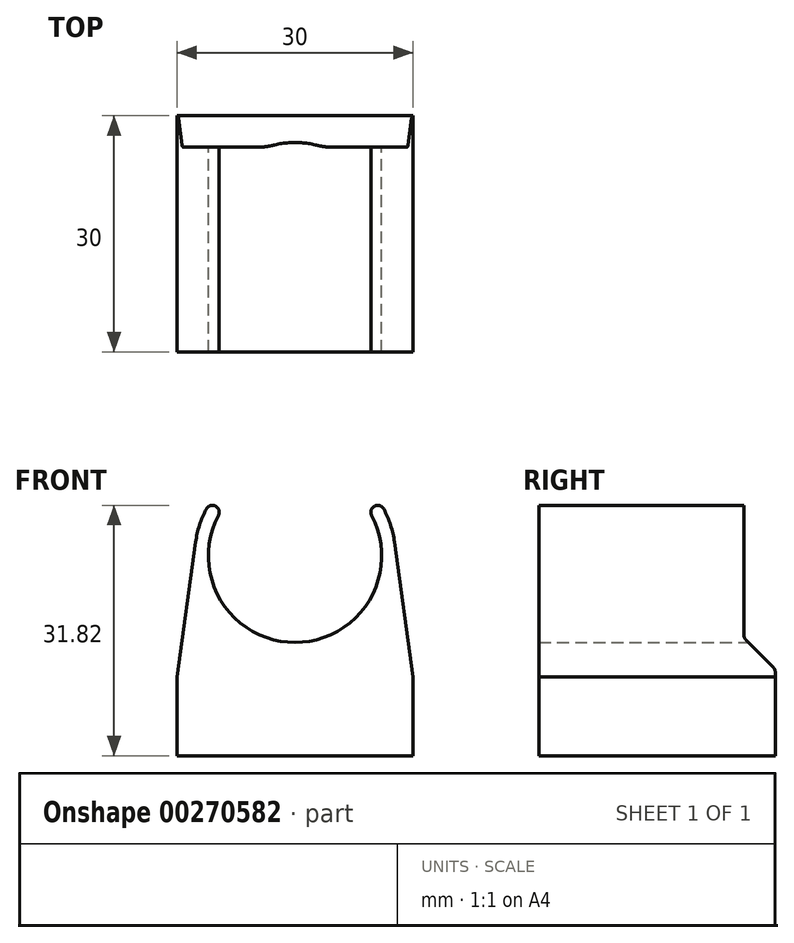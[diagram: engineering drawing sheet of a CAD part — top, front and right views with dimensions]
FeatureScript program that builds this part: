
annotation { "Feature Type Name" : "Feature", "Feature Type Description" : "" }
export const myFeature = defineFeature(function(context is Context, id is Id, definition is map)
    precondition{}
    {
        {
            var Q0;
            Q0=qCreatedBy(makeId("Front.planeOp"),FACE);
            var sketch = newSketch(context, id + "F0", { "sketchPlane" : qUnion([Q0])});
            skLineSegment(sketch, "E0.bottom", {"start": v(-15, 0) * mm, "end": v(15, 0) * mm});
            skLineSegment(sketch, "E0.top", {"start": v(-15, 10) * mm, "end": v(15, 10) * mm, "construction": true});
            skLineSegment(sketch, "E0.left", {"start": v(-15, 0) * mm, "end": v(-15, 10) * mm});
            skLineSegment(sketch, "E0.right", {"start": v(15, 0) * mm, "end": v(15, 10) * mm});
            skLineSegment(sketch, "E1", {"start": v(0, 10) * mm, "end": v(0, 14.4) * mm, "construction": true});
            skPoint(sketch, "E1.endSnap0", {"position": v(0, 10) * mm});
            skArc(sketch, "E2", {"start": v(-9.73, 30.54) * mm, "mid": v(0, 14.4) * mm, "end": v(9.73, 30.54) * mm});
            skArc(sketch, "E3", {"start": v(12.63, 27.15) * mm, "mid": v(12.14, 29.3) * mm, "end": v(11.27, 31.36) * mm});
            skLineSegment(sketch, "E4", {"start": v(-15, 10) * mm, "end": v(-12.63, 27.15) * mm});
            skLineSegment(sketch, "E5", {"start": v(15, 10) * mm, "end": v(12.63, 27.15) * mm});
            skArc(sketch, "E6", {"start": v(-9.73, 30.54) * mm, "mid": v(-10.1, 31.72) * mm, "end": v(-11.27, 31.36) * mm});
            skArc(sketch, "E7", {"start": v(11.27, 31.36) * mm, "mid": v(10.1, 31.72) * mm, "end": v(9.73, 30.54) * mm});
            skLineSegment(sketch, "E8", {"start": v(-9.63, 35.6) * mm, "end": v(-9.63, 27.49) * mm, "construction": true});
            skLineSegment(sketch, "E9", {"start": v(9.62, 38.1) * mm, "end": v(9.62, 26.4) * mm, "construction": true});
            skArc(sketch, "E10.trimOffspring", {"start": v(-11.27, 31.36) * mm, "mid": v(-12.14, 29.3) * mm, "end": v(-12.63, 27.15) * mm});
            skSolve(sketch);
        }
        {
            var Q0;
            Q0 = qSketchRegion(id + "F0", true);
            extrude(context, id + "F1", {"entities" : qUnion([Q0]), "depth" : 26 * mm});
        }
        {
            var Q0;
            Q0=makeQuery(id+"F1.opExtrude","CAP_FACE",FACE,{"disambiguationData":[OSD([sQuery(id+"F0.wireOp",EDGE,"E0.bottom"),sQuery(id+"F0.wireOp",EDGE,"E0.left"),sQuery(id+"F0.wireOp",EDGE,"E0.right"),sQuery(id+"F0.wireOp",EDGE,"E2"),sQuery(id+"F0.wireOp",EDGE,"E3"),sQuery(id+"F0.wireOp",EDGE,"E4"),sQuery(id+"F0.wireOp",EDGE,"E5"),sQuery(id+"F0.wireOp",EDGE,"E6"),sQuery(id+"F0.wireOp",EDGE,"E7"),sQuery(id+"F0.wireOp",EDGE,"E10.trimOffspring")])],"isStart":true});
            var sketch = newSketch(context, id + "F2", { "sketchPlane" : qUnion([Q0])});
            skLineSegment(sketch, "E11.0", {"start": v(15, 0) * mm, "end": v(-15, 0) * mm});
            skLineSegment(sketch, "E12.0", {"start": v(15, 0) * mm, "end": v(15, 10) * mm});
            skLineSegment(sketch, "E13.0", {"start": v(15, 10) * mm, "end": v(14.3, 15) * mm});
            skLineSegment(sketch, "E14.0", {"start": v(-15, 10) * mm, "end": v(-14.3, 15) * mm});
            skLineSegment(sketch, "E15.0", {"start": v(-15, 0) * mm, "end": v(-15, 10) * mm});
            skArc(sketch, "E16.0", {"start": v(3.58, 15) * mm, "mid": v(0, 14.4) * mm, "end": v(-3.58, 15) * mm});
            skLineSegment(sketch, "E17", {"start": v(-14.3, 15) * mm, "end": v(-3.58, 15) * mm});
            skPoint(sketch, "E18.orphan", {"position": v(-9.73, 30.54) * mm});
            skPoint(sketch, "E19.orphan", {"position": v(-12.63, 27.15) * mm});
            skLineSegment(sketch, "E20.trimOffspring", {"start": v(3.58, 15) * mm, "end": v(14.3, 15) * mm});
            skPoint(sketch, "E21.orphan", {"position": v(9.73, 30.54) * mm});
            skPoint(sketch, "E22.orphan", {"position": v(12.63, 27.15) * mm});
            skSolve(sketch);
        }
        {
            var Q0;
            Q0 = qSketchRegion(id + "F2", true);
            extrude(context, id + "F3", {"entities" : qUnion([Q0]), "operationType" : NewBodyOperationType.ADD, "depth" : 4 * mm});
        }
        {
            var Q0;
            Q0=makeQuery(id+"F3.opExtrude","CAP_EDGE",EDGE,{"disambiguationData":[OSD([sQuery(id+"F2.wireOp",EDGE,"E20.trimOffspring")])],"isStart":false});
            chamfer(context, id + "F4", {"entities" : qUnion([Q0]), "width" : 4 * mm, "tangentPropagation" : true});
        }
        {
            var Q0;
            {var subQ0=sQuery(id+"F0.wireOp",EDGE,"E7");var subQ1=sQuery(id+"F0.wireOp",EDGE,"E5");var subQ2=sQuery(id+"F0.wireOp",EDGE,"E3");var subQ3=sQuery(id+"F0.wireOp",EDGE,"E2");Q0=makeQuery(id+"F4.opChamfer","BLEND_EDGE",EDGE,{"blendedFrom":[makeQuery(id+"F3.opExtrude","CAP_EDGE",EDGE,{"disambiguationData":[OSD([sQuery(id+"F2.wireOp",EDGE,"E20.trimOffspring")])],"isStart":false}),makeQuery(id+"F3.boolean.opBoolean","SPLIT",FACE,{"disambiguationData":[TD([makeQuery(id+"F1.opExtrude","SWEPT_FACE",FACE,{"disambiguationData":[OSD([subQ2])]})])],"derivedFrom":makeQuery(id+"F1.opExtrude","CAP_FACE",FACE,{"disambiguationData":[OSD([sQuery(id+"F0.wireOp",EDGE,"E0.bottom"),sQuery(id+"F0.wireOp",EDGE,"E0.left"),sQuery(id+"F0.wireOp",EDGE,"E0.right"),subQ3,subQ2,sQuery(id+"F0.wireOp",EDGE,"E4"),subQ1,sQuery(id+"F0.wireOp",EDGE,"E6"),subQ0,sQuery(id+"F0.wireOp",EDGE,"E10.trimOffspring")])],"isStart":true})})],"blendedInto":[makeQuery(id+"F3.boolean.opBoolean","SPLIT",FACE,{"disambiguationData":[TD([makeQuery(id+"F1.opExtrude","SWEPT_FACE",FACE,{"disambiguationData":[OSD([subQ2])]})])],"derivedFrom":makeQuery(id+"F1.opExtrude","CAP_FACE",FACE,{"disambiguationData":[OSD([sQuery(id+"F0.wireOp",EDGE,"E0.bottom"),sQuery(id+"F0.wireOp",EDGE,"E0.left"),sQuery(id+"F0.wireOp",EDGE,"E0.right"),subQ3,subQ2,sQuery(id+"F0.wireOp",EDGE,"E4"),subQ1,sQuery(id+"F0.wireOp",EDGE,"E6"),subQ0,sQuery(id+"F0.wireOp",EDGE,"E10.trimOffspring")])],"isStart":true})})]});}
            fillet(context, id + "F5", {"entities" : qUnion([Q0]), "radius" : 1 * mm, "tangentPropagation" : true, "allowEdgeOverflow" : false});
        }
        {
            var Q0;
            {var subQ0=sQuery(id+"F0.wireOp",EDGE,"E10.trimOffspring");var subQ1=sQuery(id+"F0.wireOp",EDGE,"E6");var subQ2=sQuery(id+"F0.wireOp",EDGE,"E4");var subQ3=sQuery(id+"F0.wireOp",EDGE,"E2");var subQ4=sQuery(id+"F2.wireOp",EDGE,"E20.trimOffspring");Q0=makeQuery(id+"F4.opChamfer","BLEND_EDGE",EDGE,{"blendedFrom":[makeQuery(id+"F3.opExtrude","CAP_EDGE",EDGE,{"disambiguationData":[OSD([subQ4])],"isStart":false}),makeQuery(id+"F3.boolean.opBoolean","SPLIT",FACE,{"disambiguationData":[TD([makeQuery(id+"F1.opExtrude","SWEPT_FACE",FACE,{"disambiguationData":[OSD([subQ2])]})])],"derivedFrom":makeQuery(id+"F1.opExtrude","CAP_FACE",FACE,{"disambiguationData":[OSD([sQuery(id+"F0.wireOp",EDGE,"E0.bottom"),sQuery(id+"F0.wireOp",EDGE,"E0.left"),sQuery(id+"F0.wireOp",EDGE,"E0.right"),subQ3,sQuery(id+"F0.wireOp",EDGE,"E3"),subQ2,sQuery(id+"F0.wireOp",EDGE,"E5"),subQ1,sQuery(id+"F0.wireOp",EDGE,"E7"),subQ0])],"isStart":true})})],"blendedInto":[makeQuery(id+"F3.boolean.opBoolean","SPLIT",FACE,{"disambiguationData":[TD([makeQuery(id+"F1.opExtrude","SWEPT_FACE",FACE,{"disambiguationData":[OSD([subQ2])]})])],"derivedFrom":makeQuery(id+"F1.opExtrude","CAP_FACE",FACE,{"disambiguationData":[OSD([sQuery(id+"F0.wireOp",EDGE,"E0.bottom"),sQuery(id+"F0.wireOp",EDGE,"E0.left"),sQuery(id+"F0.wireOp",EDGE,"E0.right"),subQ3,sQuery(id+"F0.wireOp",EDGE,"E3"),subQ2,sQuery(id+"F0.wireOp",EDGE,"E5"),subQ1,sQuery(id+"F0.wireOp",EDGE,"E7"),subQ0])],"isStart":true})})]});}
            fillet(context, id + "F6", {"entities" : qUnion([Q0]), "radius" : 1 * mm, "tangentPropagation" : true, "allowEdgeOverflow" : false});
        }
        {
            var Q0;
            {var subQ0=sQuery(id+"F2.wireOp",EDGE,"E20.trimOffspring");Q0=makeQuery(id+"F4.opChamfer","BLEND_EDGE",EDGE,{"blendedFrom":[makeQuery(id+"F3.opExtrude","CAP_EDGE",EDGE,{"disambiguationData":[OSD([subQ0])],"isStart":false}),makeQuery(id+"F3.opExtrude","CAP_FACE",FACE,{"disambiguationData":[OSD([sQuery(id+"F2.wireOp",EDGE,"E11.0"),sQuery(id+"F2.wireOp",EDGE,"E12.0"),sQuery(id+"F2.wireOp",EDGE,"E13.0"),sQuery(id+"F2.wireOp",EDGE,"E14.0"),sQuery(id+"F2.wireOp",EDGE,"E15.0"),sQuery(id+"F2.wireOp",EDGE,"E16.0"),sQuery(id+"F2.wireOp",EDGE,"E17"),subQ0])],"isStart":false})],"blendedInto":[makeQuery(id+"F3.opExtrude","CAP_FACE",FACE,{"disambiguationData":[OSD([sQuery(id+"F2.wireOp",EDGE,"E11.0"),sQuery(id+"F2.wireOp",EDGE,"E12.0"),sQuery(id+"F2.wireOp",EDGE,"E13.0"),sQuery(id+"F2.wireOp",EDGE,"E14.0"),sQuery(id+"F2.wireOp",EDGE,"E15.0"),sQuery(id+"F2.wireOp",EDGE,"E16.0"),sQuery(id+"F2.wireOp",EDGE,"E17"),subQ0])],"isStart":false})]});}
            fillet(context, id + "F7", {"entities" : qUnion([Q0]), "radius" : 1 * mm, "tangentPropagation" : true, "allowEdgeOverflow" : false});
        }
    });
